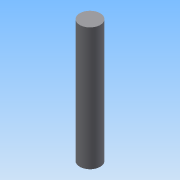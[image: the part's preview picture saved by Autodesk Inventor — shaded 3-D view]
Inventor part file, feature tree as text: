
AUTODESK INVENTOR PART (.ipt)
format: ipt  version: 2015 (Build 190159000, 159)  size: 63,488 bytes
history: native  units: mm
features: other x1, extrude x1, sketch x1
ambient origin geometry x8: Origin, YZ Plane, XZ Plane, XY Plane, X Axis, Y Axis, Z Axis, Center Point
bodies: Body1 (feature_tree)
feature tree (3):
  other  "實體1"
  extrude  "擠出1"  Depth=1.0mm
  sketch  "草圖1"
